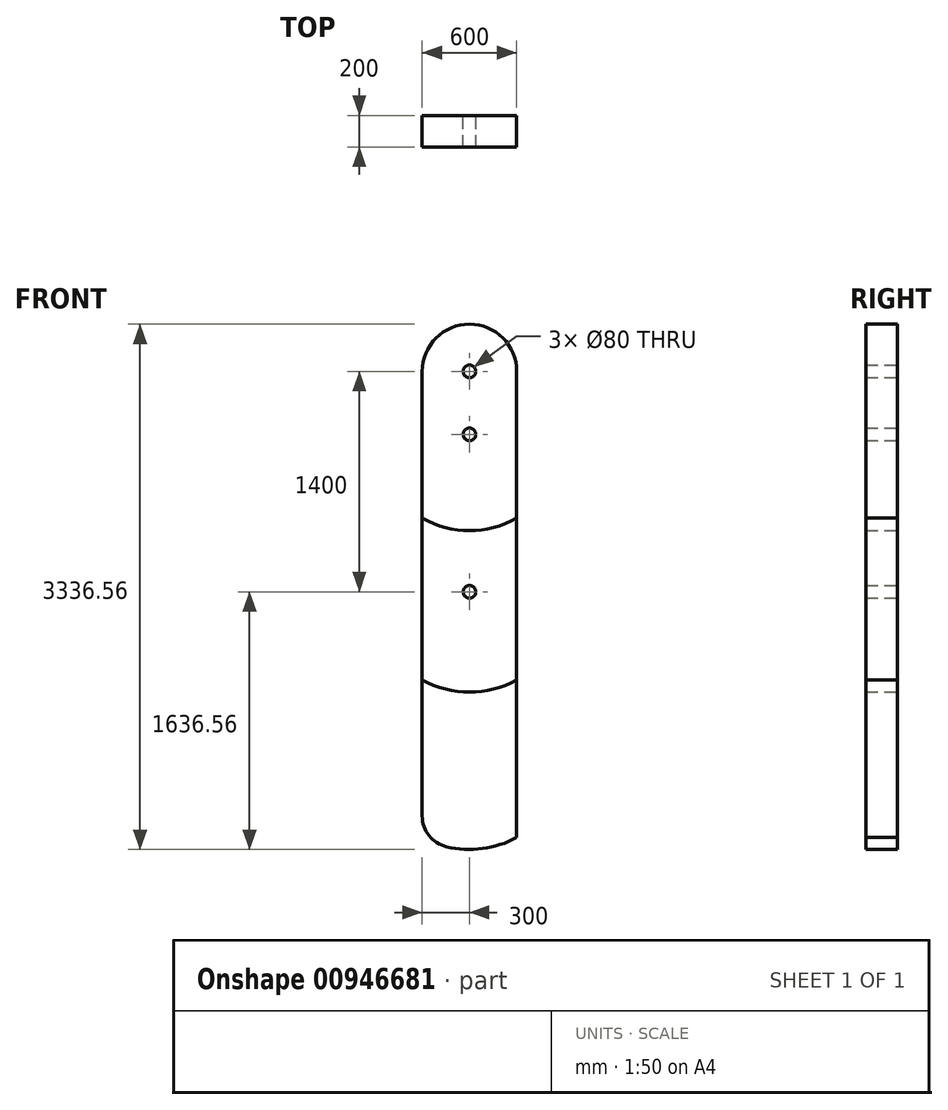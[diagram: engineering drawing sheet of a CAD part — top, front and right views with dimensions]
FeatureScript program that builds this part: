
annotation { "Feature Type Name" : "Feature", "Feature Type Description" : "" }
export const myFeature = defineFeature(function(context is Context, id is Id, definition is map)
    precondition{}
    {
        {
            var Q0;
            Q0=qCreatedBy(makeId("Front.planeOp"),FACE);
            var sketch = newSketch(context, id + "F0", { "sketchPlane" : qUnion([Q0])});
            skArc(sketch, "E0", {"start": v(300, 0) * mm, "mid": v(0, 300) * mm, "end": v(-300, 0) * mm});
            skLineSegment(sketch, "E1", {"start": v(0, 0) * mm, "end": v(0, -2500) * mm, "construction": true});
            skLineSegment(sketch, "E2", {"start": v(-111.88, -400) * mm, "end": v(0, -400) * mm, "construction": true});
            skLineSegment(sketch, "E3", {"start": v(-111.88, -1400) * mm, "end": v(0, -1400) * mm, "construction": true});
            skLineSegment(sketch, "E4", {"start": v(300, 0) * mm, "end": v(300, -2961.44) * mm});
            skArc(sketch, "E5", {"start": v(-145.81, -3019.64) * mm, "mid": v(82.4, -3031.2) * mm, "end": v(300, -2961.44) * mm});
            skLineSegment(sketch, "E6", {"start": v(-300, 0) * mm, "end": v(-300, -2824.96) * mm});
            skPoint(sketch, "E7.orphan", {"position": v(88.5, -400) * mm});
            skPoint(sketch, "E8.orphan", {"position": v(88.5, -1400) * mm});
            skArc(sketch, "E9.trimOffspring", {"start": v(-300, -932.95) * mm, "mid": v(0, -1011.58) * mm, "end": v(300, -932.95) * mm});
            skArc(sketch, "E10.trimOffspring", {"start": v(-300, -1961.44) * mm, "mid": v(0, -2036.56) * mm, "end": v(300, -1961.44) * mm});
            skCircle(sketch, "E11", {"center": v(0, 0) * mm, "radius": 40 * mm});
            skCircle(sketch, "E12", {"center": v(0, -400) * mm, "radius": 40 * mm});
            skCircle(sketch, "E13", {"center": v(0, -1400) * mm, "radius": 40 * mm});
            skPoint(sketch, "E14.visualSharp", {"position": v(-300, -2961.44) * mm});
            skArc(sketch, "E14.filletArc", {"start": v(-300, -2824.96) * mm, "mid": v(-256.78, -2949.13) * mm, "end": v(-145.81, -3019.64) * mm});
            skSolve(sketch);
        }
        {
            var Q0;
            {var subQ2=sQuery(id+"F0.wireOp",EDGE,"E0");Q0=makeQuery(id+"F0.imprint","IMPRINT",FACE,{"disambiguationData":[TD([[makeQuery(id+"F0.imprint","IMPRINT",EDGE,{"derivedFrom":subQ2}),1.0]])]});}
            extrude(context, id + "F1", {"entities" : qUnion([Q0]), "endBound" : BoundingType.SYMMETRIC, "depth" : 200 * mm, "offsetDistance" : 25 * mm});
        }
        {
            var Q0;
            {var subQ1=sQuery(id+"F0.wireOp",EDGE,"E9.trimOffspring");Q0=makeQuery(id+"F0.imprint","IMPRINT",FACE,{"disambiguationData":[TD([[makeQuery(id+"F0.imprint","IMPRINT",EDGE,{"derivedFrom":subQ1}),-1.0]])]});}
            extrude(context, id + "F2", {"entities" : qUnion([Q0]), "endBound" : BoundingType.SYMMETRIC, "depth" : 200 * mm, "offsetDistance" : 25 * mm});
        }
        {
            var Q0;
            {var subQ3=sQuery(id+"F0.wireOp",EDGE,"E5");Q0=makeQuery(id+"F0.imprint","IMPRINT",FACE,{"disambiguationData":[TD([[makeQuery(id+"F0.imprint","IMPRINT",EDGE,{"derivedFrom":subQ3}),1.0]])]});}
            extrude(context, id + "F3", {"entities" : qUnion([Q0]), "endBound" : BoundingType.SYMMETRIC, "depth" : 200 * mm, "offsetDistance" : 25 * mm});
        }
    });
